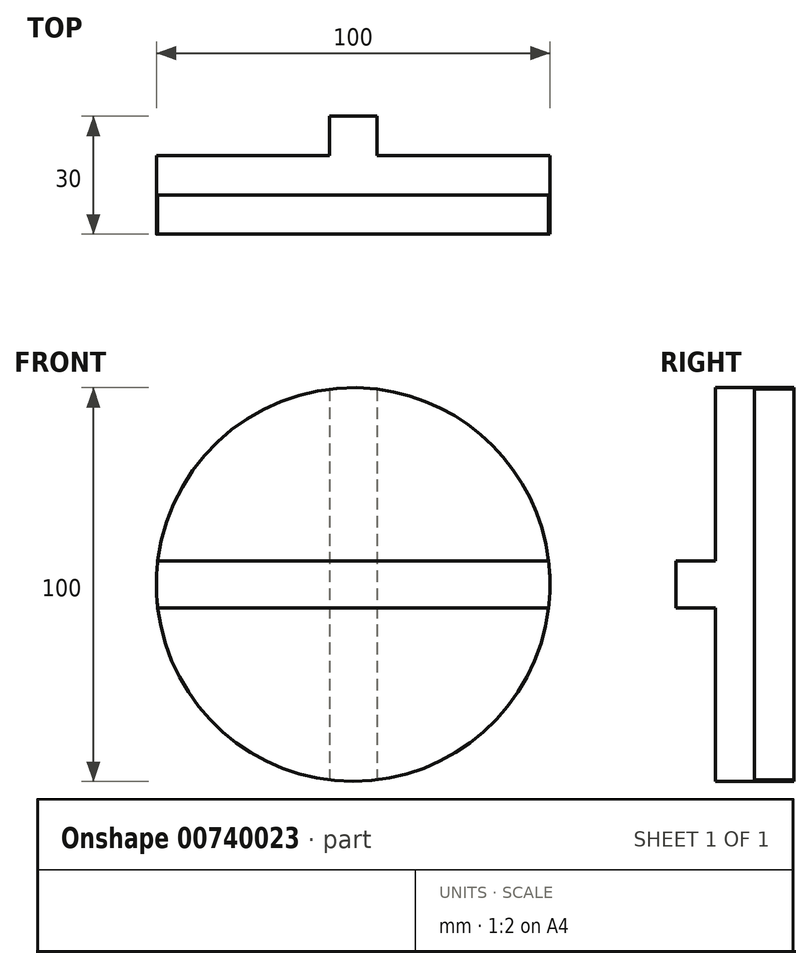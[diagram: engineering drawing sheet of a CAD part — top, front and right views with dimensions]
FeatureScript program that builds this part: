
annotation { "Feature Type Name" : "Feature", "Feature Type Description" : "" }
export const myFeature = defineFeature(function(context is Context, id is Id, definition is map)
    precondition{}
    {
        {
            var Q0;
            Q0=qCreatedBy(makeId("Front.planeOp"),FACE);
            var sketch = newSketch(context, id + "F0", { "sketchPlane" : qUnion([Q0])});
            skCircle(sketch, "E0", {"center": v(0, 0) * mm, "radius": 50 * mm});
            skSolve(sketch);
        }
        {
            var Q0;
            Q0=makeQuery(id+"F0.imprint","IMPRINT",FACE,{"disambiguationData":[TD([[makeQuery(id+"F0.imprint","IMPRINT",EDGE,{"derivedFrom":sQuery(id+"F0.wireOp",EDGE,"E0")}),1.0]])]});
            extrude(context, id + "F1", {"entities" : qUnion([Q0]), "depth" : 10 * mm, "offsetDistance" : 25 * mm});
        }
        {
            var Q0;
            Q0=makeQuery(id+"F1.opExtrude","CAP_FACE",FACE,{"disambiguationData":[OSD([sQuery(id+"F0.wireOp",EDGE,"E0")])],"isStart":false});
            var sketch = newSketch(context, id + "F2", { "sketchPlane" : qUnion([Q0])});
            skLineSegment(sketch, "E1.bottom", {"start": v(-49.64, 6) * mm, "end": v(49.64, 6) * mm});
            skLineSegment(sketch, "E1.top", {"start": v(-49.64, -6) * mm, "end": v(49.64, -6) * mm});
            skPoint(sketch, "E1.middle", {"position": v(0, 0) * mm});
            skArc(sketch, "E2", {"start": v(-49.64, 6) * mm, "mid": v(-50, 0) * mm, "end": v(-49.64, -6) * mm});
            skArc(sketch, "E3.trimOffspring", {"start": v(49.64, -6) * mm, "mid": v(50, 0) * mm, "end": v(49.64, 6) * mm});
            skSolve(sketch);
        }
        {
            var Q0;
            Q0=makeQuery(id+"F2.imprint","IMPRINT",FACE,{"disambiguationData":[TD([[makeQuery(id+"F2.imprint","IMPRINT",EDGE,{"derivedFrom":sQuery(id+"F2.wireOp",EDGE,"E1.bottom")}),-1.0]])]});
            extrude(context, id + "F3", {"entities" : qUnion([Q0]), "operationType" : NewBodyOperationType.ADD, "depth" : 10 * mm, "offsetDistance" : 25 * mm});
        }
        {
            var Q0;
            Q0=qCreatedBy(makeId("Front.planeOp"),FACE);
            var sketch = newSketch(context, id + "F4", { "sketchPlane" : qUnion([Q0])});
            skLineSegment(sketch, "E4.left", {"start": v(6, 49.64) * mm, "end": v(6, -49.64) * mm});
            skLineSegment(sketch, "E4.right", {"start": v(-6, 49.64) * mm, "end": v(-6, -49.64) * mm});
            skPoint(sketch, "E4.middle", {"position": v(0, 0) * mm});
            skArc(sketch, "E5", {"start": v(6, 49.64) * mm, "mid": v(0, 50) * mm, "end": v(-6, 49.64) * mm});
            skArc(sketch, "E6.trimOffspring", {"start": v(-6, -49.64) * mm, "mid": v(0, -50) * mm, "end": v(6, -49.64) * mm});
            skSolve(sketch);
        }
        {
            var Q0;
            Q0=makeQuery(id+"F4.imprint","IMPRINT",FACE,{"disambiguationData":[TD([[makeQuery(id+"F4.imprint","IMPRINT",EDGE,{"derivedFrom":sQuery(id+"F4.wireOp",EDGE,"E4.left")}),-1.0]])]});
            extrude(context, id + "F5", {"entities" : qUnion([Q0]), "operationType" : NewBodyOperationType.ADD, "oppositeDirection" : true, "depth" : 10 * mm, "offsetDistance" : 25 * mm});
        }
    });
